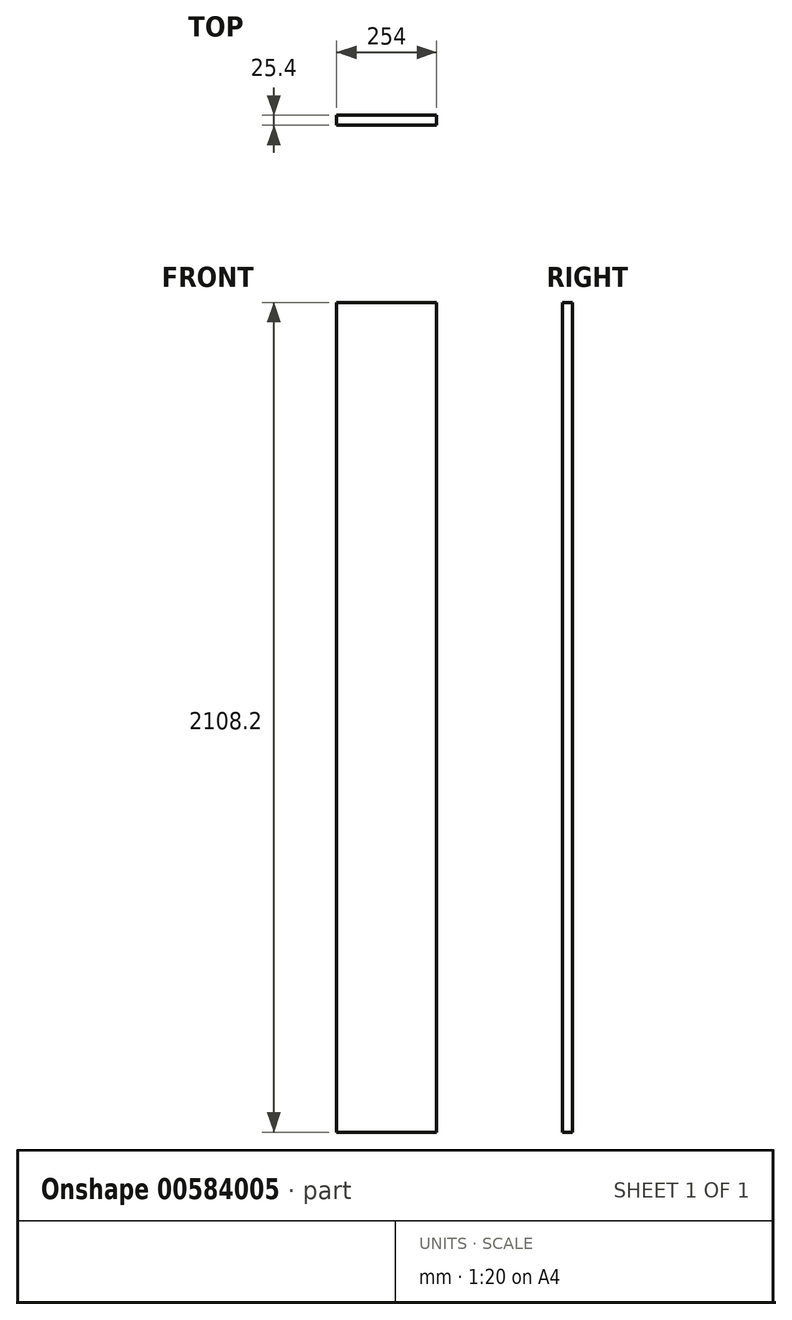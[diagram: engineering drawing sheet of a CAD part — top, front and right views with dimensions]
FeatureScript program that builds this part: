
annotation { "Feature Type Name" : "Feature", "Feature Type Description" : "" }
export const myFeature = defineFeature(function(context is Context, id is Id, definition is map)
    precondition{}
    {
        {
            var Q0;
            Q0=qCreatedBy(makeId("Front.planeOp"),FACE);
            var sketch = newSketch(context, id + "F0", { "sketchPlane" : qUnion([Q0])});
            skLineSegment(sketch, "E0.bottom", {"start": v(0, -316.46) * mm, "end": v(-254, -316.46) * mm});
            skLineSegment(sketch, "E0.top", {"start": v(0, 1791.74) * mm, "end": v(-254, 1791.74) * mm});
            skLineSegment(sketch, "E0.left", {"start": v(0, -316.46) * mm, "end": v(0, 1791.74) * mm});
            skLineSegment(sketch, "E0.right", {"start": v(-254, -316.46) * mm, "end": v(-254, 1791.74) * mm});
            skPoint(sketch, "E0.middle", {"position": v(-127, 737.64) * mm});
            skLineSegment(sketch, "E1", {"start": v(-254, -291.06) * mm, "end": v(0, -291.06) * mm, "construction": true});
            skSolve(sketch);
        }
        {
            var Q0;
            Q0=makeQuery(id+"F0.imprint","IMPRINT",FACE,{"disambiguationData":[TD([[makeQuery(id+"F0.imprint","IMPRINT",EDGE,{"derivedFrom":sQuery(id+"F0.wireOp",EDGE,"E0.bottom")}),-1.0]])]});
            extrude(context, id + "F1", {"entities" : qUnion([Q0]), "depth" : 25.4 * mm, "offsetDistance" : 25.4 * mm});
        }
    });
